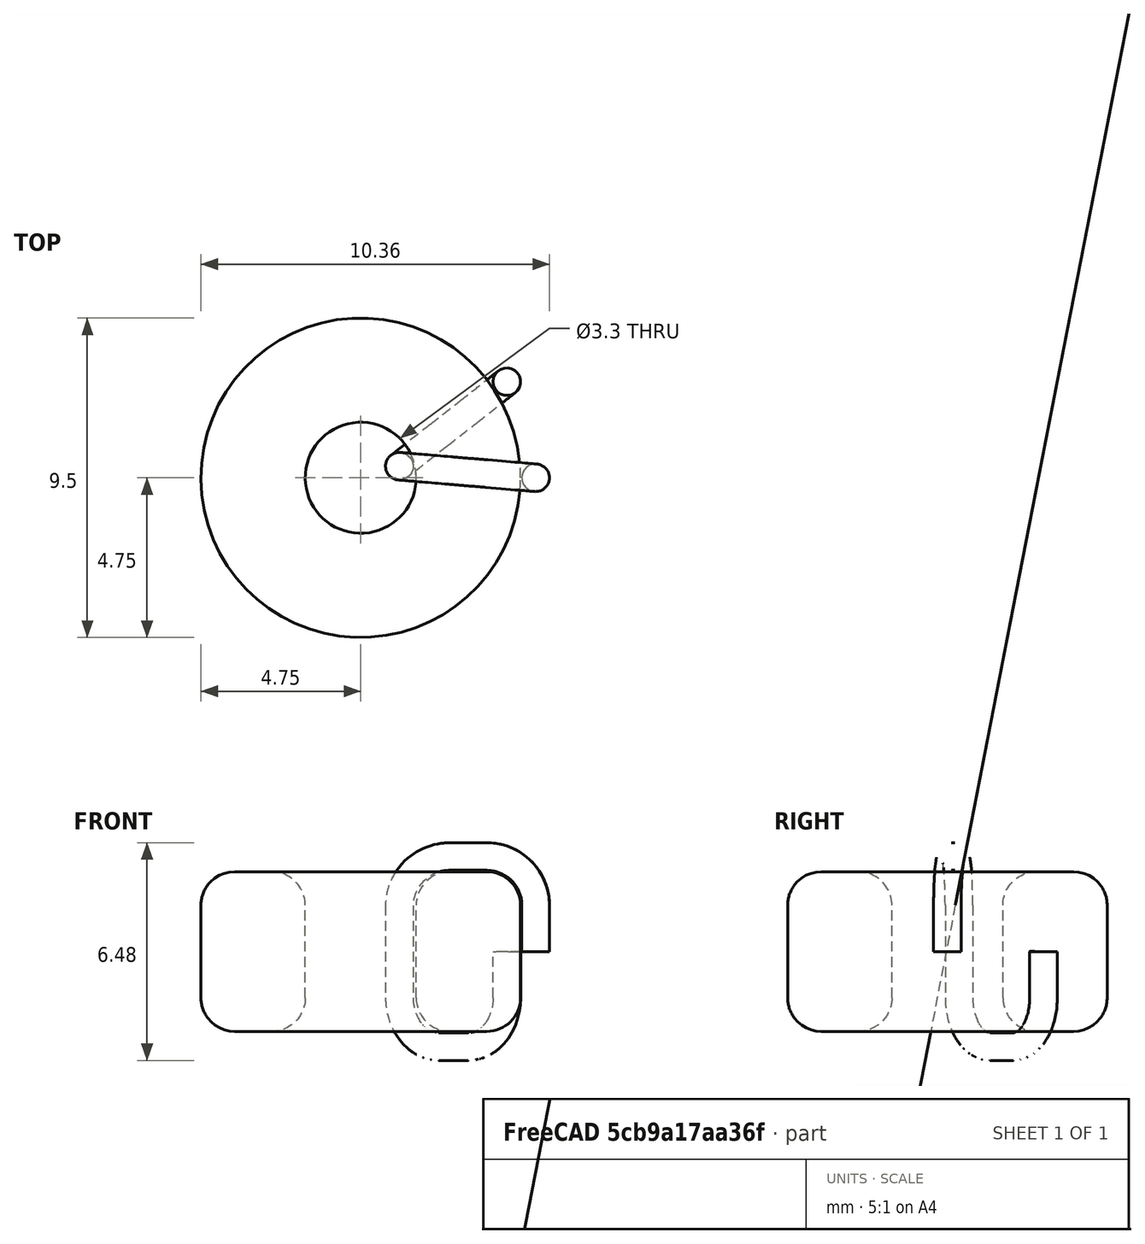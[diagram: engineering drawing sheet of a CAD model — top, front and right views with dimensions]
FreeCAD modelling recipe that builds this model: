
FCSTD DOCUMENT  (FreeCAD 0.19R24415 (Git))
Label: toroid
License: All rights reserved
LicenseURL: http://en.wikipedia.org/wiki/All_rights_reserved
objects: Sketcher::SketchObject×5, PartDesign::Body×3, PartDesign::Revolution×2, App::Part×2, Part::Extrusion×2, Part::Sweep×2, Part::FeaturePython×2, Spreadsheet::Sheet×1, Part::MultiFuse×1, Part::Section×1, Part::Circle×1, PartDesign::FeatureBase×1
note: 20 computed .brp shape members not serialized (recipe doc carries the construction recipe); baked Part::Feature solids carry a one-line shape summary decoded from their .brp

FEATURE [Spreadsheet::Sheet] Spreadsheet  label="SET"
  cells = F1=TOROID PARAMETERRS; F2=DESCRIPTION; G2=VALUE; H2=UNIT; A3=Wire diameter; B3(L2_wd)=0.82; C3=mm; F3=Torus Outside Diameter OD; G3(T_OD)=9.5; H3=mm; A4=Fill angle; B4(L2_fa)=300; C4=# 0 <= fa <= 360; F4=Torus Inside Diameter ID; G4(T_ID)=3.3; H4=mm; A5=Turns; B5(L2_n)=10; F5=Torus cross-section Height; G5(T_H)=4.75; H5=mm; A6=Wire radius; B6(L2_wr)==L2_wd / 2; C6(L02_wr)==L2_wd / 2; F6=Torus cross-section Fillet; G6(T_F)=1; H6=mm; A7=Winding gap; B7(L2_wg)==L2_wd * 0.05; C7(L02_wg)==L2_wd * 0.05; F7=Torus cross-section Width; G7(T_W)==(T_OD - T_ID) / 2; H7=mm; A8=start angle; B8(L2_sa)==(360 - L2_fa) / 4; C8=# 0 <= sa <= 360; F8=Torus minor radius; G8(T_r1)==T_ID / 2; H8=mm; A9=inside radius; B9(L2_iwo)==L02_wr + L02_wg; C9=mm; F9=Torus major radius; G9(T_R2)==T_OD / 2; H9=mm; A10=outside radius; B10(L2_owo)==L02_wr + L02_wg; C10=mm; F10=Torus median radius; G10(T_Rm)==(T_r1 + T_R2) / 2; H10=mm
FEATURE [Sketcher::SketchObject] Sketch  label="Sketch_Torus"
  FullyConstrained = true
  MapMode = 5
  Placement = pos=(0,0,0) rot=(1,0,0;1.5708rad)
  Support = -> [XZ_Plane001]
  expr: Constraints[19] = <<SET>>.T_r1
  expr: Constraints[20] = <<SET>>.T_R2
  expr: Constraints[21] = <<SET>>.T_H
  expr: Constraints[22] = <<SET>>.T_F
  sketch-geometry (10):
    g0: LineSegment StartX=1.65 StartY=-1.375 StartZ=0 EndX=1.65 EndY=1.375 EndZ=0
    g1: LineSegment StartX=2.65 StartY=2.375 StartZ=0 EndX=3.75 EndY=2.375 EndZ=0
    g2: LineSegment StartX=4.75 StartY=1.375 StartZ=0 EndX=4.75 EndY=-1.375 EndZ=0
    g3: LineSegment StartX=3.75 StartY=-2.375 StartZ=0 EndX=2.65 EndY=-2.375 EndZ=0
    g4: ArcOfCircle CenterX=2.65 CenterY=1.375 CenterZ=0 NormalX=0 NormalY=0 NormalZ=1 AngleXU=0 Radius=1 StartAngle=1.5708 EndAngle=3.14159
    g5: ArcOfCircle CenterX=3.75 CenterY=1.375 CenterZ=0 NormalX=0 NormalY=0 NormalZ=1 AngleXU=0 Radius=1 StartAngle=1e-16 EndAngle=1.5708
    g6: ArcOfCircle CenterX=3.75 CenterY=-1.375 CenterZ=0 NormalX=0 NormalY=0 NormalZ=1 AngleXU=0 Radius=1 StartAngle=4.71239 EndAngle=6.28319
    g7: ArcOfCircle CenterX=2.65 CenterY=-1.375 CenterZ=0 NormalX=0 NormalY=0 NormalZ=1 AngleXU=0 Radius=1 StartAngle=3.14159 EndAngle=4.71239
    g8: LineSegment StartX=1.65 StartY=1.375 StartZ=0 EndX=0 EndY=2e-16 EndZ=0
    g9: LineSegment StartX=1.65 StartY=-1.375 StartZ=0 EndX=0 EndY=2e-16 EndZ=0
  constraints (24):
    c: Vertical(g0)
    c: Horizontal(g1)
    c: Horizontal(g3)
    c: Tangent(g0,g4) = 1.5708
    c: Tangent(g1,g4) = 1.5708
    c: Tangent(g1,g5) = 1.5708
    c: Tangent(g2,g5) = 1.5708
    c: Tangent(g2,g6) = 1.5708
    c: Tangent(g3,g6) = 1.5708
    c: Tangent(g3,g7) = 1.5708
    c: Tangent(g0,g7) = 1.5708
    c: Coincident(g9,g-1)
    c: Coincident(g9,g8)
    c: Coincident(g0,g8)
    c: Coincident(g9,g0)
    c: Equal(g8,g9)
    c: Vertical(g2)
    c: Equal(g7,g4)
    c: Equal(g5,g6)
    c: DistanceX(g-1,g0) = 1.65
    c: DistanceX(g-1,g2) = 4.75
    c: DistanceY(g3,g1) = 4.75
    c: Radius(g4) = 1
    c: Equal(g7,g6)
FEATURE [PartDesign::Revolution] Revolution  label="Revolution_Torus"
  Angle = 360
  Axis = (0,-2e-16,1)
  Base = (0,0,0)
  Placement = pos=(0,0,0) rot=(1,0,0;1.5708rad)
  Profile = -> Sketch
  ReferenceAxis = -> Sketch [V_Axis]
  Reversed = true
FEATURE [PartDesign::Body] Body  label="Body_Torus"
  Group = -> [Sketch,Revolution]
  Origin = -> Origin001
  Tip = -> Revolution
FEATURE [App::Part] Part  label="Part_Torus"
  Group = -> [Body]
  Origin = -> Origin
FEATURE [Sketcher::SketchObject] Sketch003  label="Sketch_Orbit_L02A"
  FullyConstrained = true
  MapMode = 5
  Placement = pos=(0,0,0) rot=(1,0,0;1.5708rad)
  expr: Constraints[22] = <<SET>>.T_r1 - Spreadsheet.L2_iwo
  expr: Constraints[27] = <<SET>>.T_H + 2 * Spreadsheet.L2_owo
  expr: Constraints[23] = <<SET>>.T_R2 + Spreadsheet.L2_owo
  expr: Constraints[24] = <<SET>>.T_F + Spreadsheet.L2_iwo
  expr: Constraints[25] = <<SET>>.T_F + Spreadsheet.L2_owo
  expr: Constraints[26] = <<SET>>.T_H + 2 * Spreadsheet.L2_iwo
  sketch-geometry (12):
    g0: LineSegment StartX=1.199 StartY=-1.375 StartZ=0 EndX=1.199 EndY=1.375 EndZ=0
    g1: LineSegment StartX=2.65 StartY=2.826 StartZ=0 EndX=3.75 EndY=2.826 EndZ=0
    g2: LineSegment StartX=5.201 StartY=1.375 StartZ=0 EndX=5.201 EndY=-1.375 EndZ=0
    g3: LineSegment StartX=3.75 StartY=-2.826 StartZ=0 EndX=2.65 EndY=-2.826 EndZ=0
    g4: ArcOfCircle CenterX=2.65 CenterY=1.375 CenterZ=0 NormalX=0 NormalY=0 NormalZ=1 AngleXU=0 Radius=1.451 StartAngle=1.5708 EndAngle=3.14159
    g5: ArcOfCircle CenterX=2.65 CenterY=-1.375 CenterZ=0 NormalX=0 NormalY=0 NormalZ=1 AngleXU=0 Radius=1.451 StartAngle=3.14159 EndAngle=4.71239
    g6: ArcOfCircle CenterX=3.75 CenterY=-1.375 CenterZ=0 NormalX=0 NormalY=0 NormalZ=1 AngleXU=0 Radius=1.451 StartAngle=4.71239 EndAngle=6.28319
    g7: ArcOfCircle CenterX=3.75 CenterY=1.375 CenterZ=0 NormalX=0 NormalY=0 NormalZ=1 AngleXU=0 Radius=1.451 StartAngle=0 EndAngle=1.5708
    g8: LineSegment StartX=1.199 StartY=1.375 StartZ=0 EndX=0 EndY=0 EndZ=0
    g9: LineSegment StartX=0 StartY=0 StartZ=0 EndX=1.199 EndY=-1.375 EndZ=0
    g10: LineSegment StartX=0 StartY=0 StartZ=0 EndX=5.201 EndY=-1.375 EndZ=0
    g11: LineSegment StartX=0 StartY=0 StartZ=0 EndX=5.201 EndY=1.375 EndZ=0
  constraints (28):
    c: Vertical(g0)
    c: Vertical(g2)
    c: Tangent(g0,g4) = 1.5708
    c: Tangent(g1,g4) = 1.5708
    c: Tangent(g0,g5) = 1.5708
    c: Tangent(g3,g5) = 1.5708
    c: Tangent(g3,g6) = 1.5708
    c: Tangent(g2,g6) = 1.5708
    c: Tangent(g1,g7) = 1.5708
    c: Tangent(g2,g7) = 1.5708
    c: Equal(g4,g5)
    c: Equal(g7,g6)
    c: Coincident(g11,g8)
    c: Coincident(g11,g-1)
    c: Coincident(g11,g9)
    c: Coincident(g11,g10)
    c: Coincident(g8,g0)
    c: Coincident(g9,g0)
    c: Coincident(g11,g2)
    c: Coincident(g10,g2)
    c: Equal(g8,g9)
    c: Equal(g11,g10)
    c: DistanceX(g-1,g0) = 1.199
    c: DistanceX(g-1,g2) = 5.201
    c: Radius(g4) = 1.451
    c: Radius(g7) = 1.451
    c: DistanceY(g3,g1) = 5.652
    c: DistanceY(g3,g1) = 5.652
FEATURE [PartDesign::Revolution] Revolution002  label="Revolution_Orbit_L02A"
  Angle = 360
  Axis = (0,2e-16,1)
  Base = (0,0,0)
  Placement = pos=(0,0,0) rot=(1,0,0;1.5708rad)
  Profile = -> Sketch003
  ReferenceAxis = -> Sketch003 [V_Axis]
  Reversed = true
FEATURE [Sketcher::SketchObject] Sketch004  label="Sketch_Orbit_Slice_L02A"
  FullyConstrained = true
  MapMode = 5
  expr: Constraints[2] = <<SET>>.T_r1 - <<SET>>.L2_iwo
  expr: Constraints[3] = <<SET>>.T_R2 + <<SET>>.L2_owo
  expr: Constraints[11] = Spreadsheet.L2_fa / (<<SET>>.L2_n > 1 ? <<SET>>.L2_n - 1 : 1) / 2
  expr: Constraints[12] = Spreadsheet.L2_fa / (<<SET>>.L2_n > 1 ? <<SET>>.L2_n - 1 : 1)
  sketch-geometry (7):
    g0: Circle CenterX=0 CenterY=0 CenterZ=0 NormalX=0 NormalY=0 NormalZ=1 AngleXU=0 Radius=1.199
    g1: Circle CenterX=0 CenterY=0 CenterZ=0 NormalX=0 NormalY=0 NormalZ=1 AngleXU=0 Radius=5.201
    g2: LineSegment StartX=0 StartY=0 StartZ=0 EndX=5.201 EndY=0 EndZ=0
    g3: LineSegment StartX=0 StartY=0 StartZ=0 EndX=1.14863 EndY=0.343877 EndZ=0
    g4: LineSegment StartX=0 StartY=0 StartZ=0 EndX=4.34537 EndY=2.858 EndZ=0
    g5: LineSegment StartX=1.14863 StartY=0.343877 StartZ=0 EndX=4.34537 EndY=2.858 EndZ=0
    g6: LineSegment StartX=1.14863 StartY=0.343877 StartZ=0 EndX=5.201 EndY=0 EndZ=0
  constraints (17):
    c: Coincident(g0,g-1)
    c: Coincident(g1,g0)
    c: Radius(g0) = 1.199
    c: Radius(g1) = 5.201
    c: Horizontal(g2)
    c: Coincident(g4,g3)
    c: Coincident(g4,g0)
    c: Coincident(g4,g2)
    c: PointOnObject(g2,g1)
    c: PointOnObject(g3,g0)
    c: PointOnObject(g4,g1)
    c: Angle(g2,g3) = 0.290888
    c: Angle(g2,g4) = 0.581776
    c: Coincident(g5,g3)
    c: Coincident(g5,g6)
    c: Coincident(g5,g4)
    c: Coincident(g6,g2)
FEATURE [Part::Extrusion] Extrude002  label="Extrude_Slice_UP_L02A"
  Base = -> Sketch004
  Dir = (0,0,1)
  DirMode = 2
  FaceMakerClass = Part::FaceMakerBullseye
  LengthFwd = 3.277
  LengthRev = 0
  Solid = false
  Symmetric = false
  expr: LengthFwd = <<SET>>.T_H / 2 + <<SET>>.L2_iwo + <<SET>>.L2_owo
FEATURE [Part::Extrusion] Extrude003  label="Extrude_Slice_DOWN_L02A"
  Base = -> Sketch004
  Dir = (0,0,1)
  DirMode = 2
  FaceMakerClass = Part::FaceMakerBullseye
  LengthFwd = 0
  LengthRev = 3.277
  Solid = false
  Symmetric = false
  expr: LengthRev = <<SET>>.T_H / 2 + Spreadsheet.L2_iwo + Spreadsheet.L2_owo
FEATURE [Part::MultiFuse] Fusion001  label="Fusion_Slice_L02A"
  Shapes = -> [Extrude002,Extrude003]
FEATURE [Part::Section] Section001  label="Section_Orbit_Slice_L02A"
  Approximation = false
  Base = -> Revolution002
  Tool = -> Fusion001
FEATURE [Part::Circle] Circle001  label="Circle_L02A"
  Angle0 = 0
  Angle1 = 360
  AttacherType = Attacher::AttachEngine3D
  Placement = pos=(5.201,0,0) rot=(0,0,1;0rad)
  Radius = 0.41
  expr: Radius = <<SET>>.L02_wr
  expr: .Placement.Base.x = <<SET>>.T_R2 + Spreadsheet.L2_owo
FEATURE [Part::Sweep] Sweep001  label="Sweep_Orbit_Slice_L02A"
  Frenet = false
  Sections = -> [Circle001]
  Solid = true
  Spine = -> Section001 [Edge8,Edge6,Edge2,Edge1,Edge4,Edge18,Edge17,Edge14,Edge13,Edge15]
  Transition = 1
FEATURE [Part::FeaturePython] Array002  label="Array_Winding_L02A"  # Draft array (typed FeaturePython)
  Angle = 300
  ArrayType = 1
  Axis = (0,0,1)
  Base = -> Sweep001
  Center = (0,0,0)
  Count = 10
  ExpandArray = false
  Fuse = false
  IntervalAxis = (0,0,0)
  IntervalX = (50,0,0)
  IntervalY = (0,50,0)
  IntervalZ = (0,0,50)
  NumberCircles = 3
  NumberPolar = 10
  NumberX = 2
  NumberY = 2
  NumberZ = 1
  Placement = pos=(0,0,0) rot=(0,0,1;0.261799rad)
  PlacementList = 10 placements: [(0,0,0),(0,0,0),(0,0,0),(0,0,0),(0,0,0),(0,0,0),(0,0,0),(0,0,0),(0,0,0),(0,0,0)]
  RadialDistance = 50
  ScaleList = (10) [(1,1,1),(1,1,1),(1,1,1),(1,1,1),(1,1,1),(1,1,1),(1,1,1),(1,1,1),(1,1,1),(1,1,1)]
  Symmetry = 1
  TangentialDistance = 25
  expr: .Placement.Rotation.Angle = Spreadsheet.L2_sa
  expr: NumberPolar = <<SET>>.L02_N
  expr: Angle = Spreadsheet.L2_fa
FEATURE [Part::FeaturePython] Array003  label="Array_Winding_L02B"  # Draft array (typed FeaturePython)
  Angle = 300
  ArrayType = 1
  Axis = (0,0,1)
  Base = -> Sweep001
  Center = (0,0,0)
  Count = 10
  ExpandArray = false
  Fuse = false
  IntervalAxis = (0,0,0)
  IntervalX = (50,0,0)
  IntervalY = (0,50,0)
  IntervalZ = (0,0,50)
  NumberCircles = 3
  NumberPolar = 10
  NumberX = 2
  NumberY = 2
  NumberZ = 1
  Placement = pos=(0,0,0) rot=(0,0,1;0.552688rad)
  PlacementList = 10 placements: [(0,0,0),(0,0,0),(0,0,0),(0,0,0),(0,0,0),(0,0,0),(0,0,0),(0,0,0),(0,0,0),(0,0,0)]
  RadialDistance = 50
  ScaleList = (10) [(1,1,1),(1,1,1),(1,1,1),(1,1,1),(1,1,1),(1,1,1),(1,1,1),(1,1,1),(1,1,1),(1,1,1)]
  Symmetry = 1
  TangentialDistance = 25
  expr: Angle = Spreadsheet.L2_fa
  expr: NumberPolar = <<SET>>.L02_N
  expr: .Placement.Rotation.Angle = Spreadsheet.L2_sa + Spreadsheet.L2_fa / (<<SET>>.L02_N > 1 ? <<SET>>.L02_N - 1 : 1) / 2
FEATURE [App::Part] Part002  label="Part_Winding_L002"
  Group = -> [Extrude003,Sketch004,Extrude002,Fusion001,Sketch003,Revolution002,Section001,Circle001,Sweep001,Array002,Array003]
  Origin = -> Origin003
FEATURE [Sketcher::SketchObject] Sketch005
  FullyConstrained = false
  MapMode = 5
  Placement = pos=(0,0,0) rot=(1,0,0;1.5708rad)
  Support = -> [XZ_Plane004]
  sketch-geometry (9):
    g0-g4: Circle x5 (B-spline internal-alignment scaffolding for g5; pole/knot coordinates omitted)
    g5: BSplineCurve PolesCount=5 KnotsCount=3 Degree=3 IsPeriodic=0
    g6: GeomPoint X=5.14534 Y=0 Z=0
    g7: GeomPoint X=9.23677 Y=-2.28869 Z=0
    g8: GeomPoint X=11.9933 Y=-2.1976 Z=0
  constraints (7):
    c: PointOnObject(g5,g-1)
    c: Weight(g0) = 1
    c: Equal(g0, g1-g4) x4
    c: InternalAlignment(g0-g4 -> g5) x5
    c: InternalAlignment(g6,g5)
    c: InternalAlignment(g7,g5)
    c: InternalAlignment(g8,g5)
FEATURE [Sketcher::SketchObject] Sketch006
  FullyConstrained = false
  MapMode = 5
  Support = -> [XY_Plane004]
  expr: Constraints[0] = Spreadsheet.L2_wd
  sketch-geometry (1):
    g0: Circle CenterX=5.14683 CenterY=-0.00283 CenterZ=0 NormalX=0 NormalY=0 NormalZ=1 AngleXU=0 Radius=0.41
  constraints (1):
    c: Diameter(g0) = 0.82
FEATURE [PartDesign::Body] Body001
  Group = -> [Sketch005,Sketch006]
  Origin = -> Origin004
FEATURE [Part::Sweep] Sweep
  Frenet = false
  Placement = pos=(-0.12,1.35,0) rot=(0,0,1;0rad)
  Sections = -> [Sketch006]
  Solid = false
  Spine = -> Sketch005 [Edge1]
  Transition = 1
FEATURE [PartDesign::FeatureBase] Clone
  BaseFeature = -> Sweep
  Placement = pos=(0.04,0.24,0) rot=(0,0,1;0rad)
FEATURE [PartDesign::Body] Body002
  BaseFeature = -> Sweep
  Group = -> [Clone]
  Origin = -> Origin005
  Placement = pos=(-0.09,-0.816622,-0.00140342) rot=(1,0,0;3.14159rad)
  Tip = -> Clone
